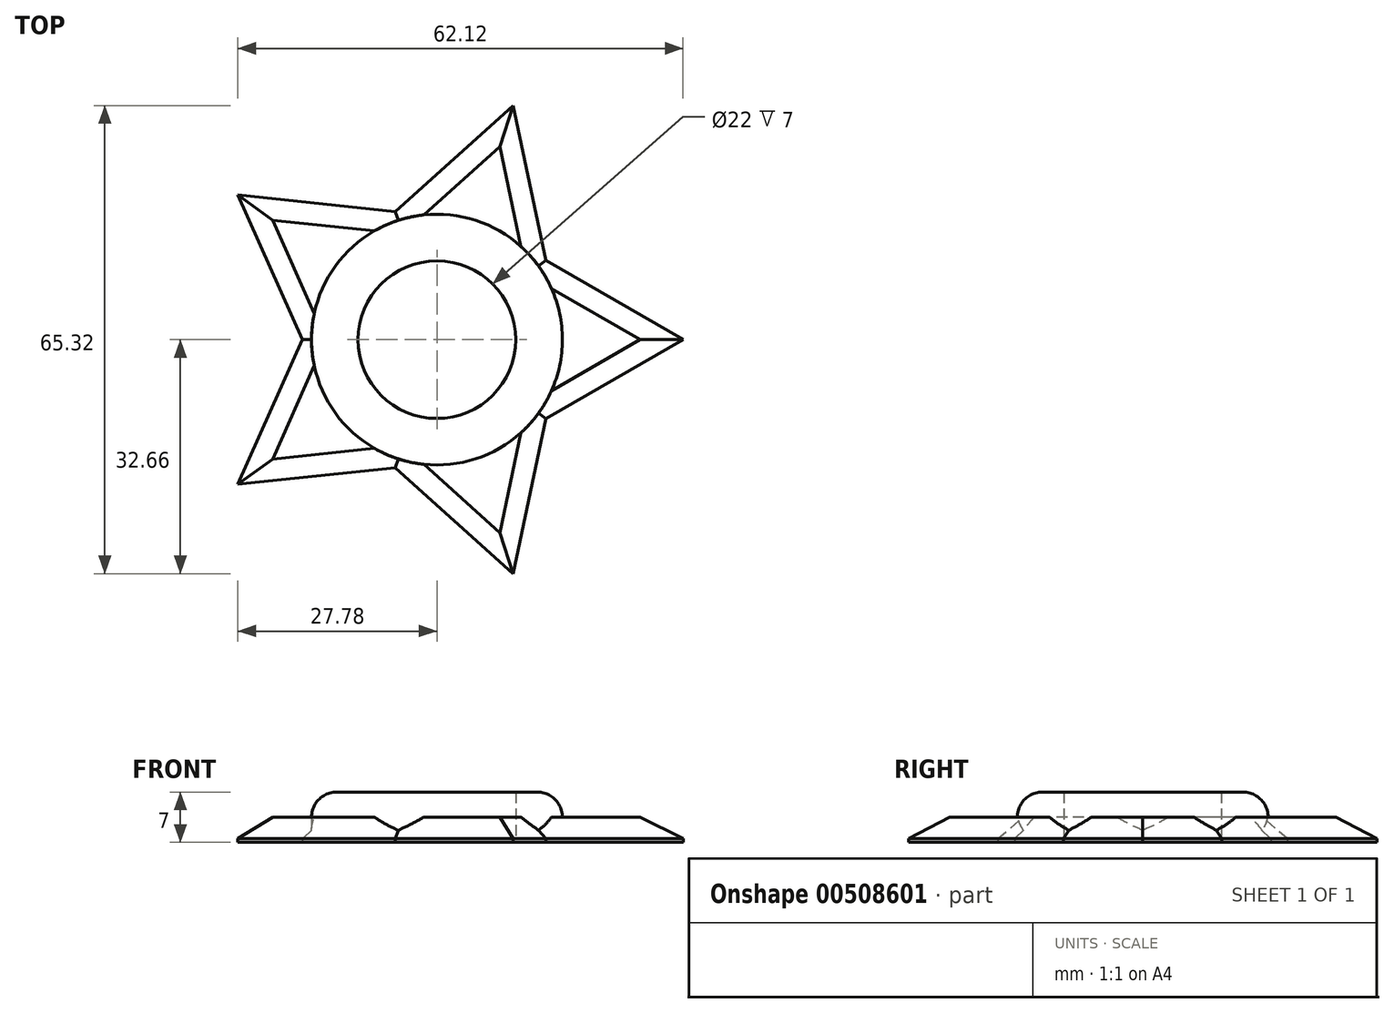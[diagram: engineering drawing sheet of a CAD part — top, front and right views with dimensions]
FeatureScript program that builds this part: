
annotation { "Feature Type Name" : "Feature", "Feature Type Description" : "" }
export const myFeature = defineFeature(function(context is Context, id is Id, definition is map)
    precondition{}
    {
        {
            var Q0;
            Q0=qCreatedBy(makeId("Top.planeOp"),FACE);
            var sketch = newSketch(context, id + "F0", { "sketchPlane" : qUnion([Q0])});
            skCircle(sketch, "E0", {"center": v(0, 0) * mm, "radius": 17.5 * mm});
            skCircle(sketch, "E1", {"center": v(0, 0) * mm, "radius": 11 * mm});
            skSolve(sketch);
        }
        {
            var Q0;
            Q0=makeQuery(id+"F0.imprint","IMPRINT",FACE,{"disambiguationData":[TD([[makeQuery(id+"F0.imprint","IMPRINT",EDGE,{"derivedFrom":sQuery(id+"F0.wireOp",EDGE,"E0")}),1.0]])]});
            extrude(context, id + "F1", {"entities" : qUnion([Q0]), "depth" : 7 * mm});
        }
        {
            var Q0;
            Q0=qCreatedBy(makeId("Top.planeOp"),FACE);
            var sketch = newSketch(context, id + "F2", { "sketchPlane" : qUnion([Q0])});
            skCircle(sketch, "E2.cCircle", {"center": v(18.8, 0) * mm, "radius": 7.77 * mm, "construction": true});
            skLineSegment(sketch, "E2.0", {"start": v(11.02, 13.46) * mm, "end": v(11.02, -13.46) * mm});
            skLineSegment(sketch, "E2.1", {"start": v(34.34, 0) * mm, "end": v(11.02, 13.46) * mm});
            skLineSegment(sketch, "E2.2", {"start": v(11.02, -13.46) * mm, "end": v(34.34, 0) * mm});
            skPoint(sketch, "E2.0.midPoint", {"position": v(11.02, 0) * mm});
            skLineSegment(sketch, "E3.1.0", {"start": v(16.21, 6.32) * mm, "end": v(10.61, 32.66) * mm});
            skLineSegment(sketch, "E3.1.1", {"start": v(10.61, 32.66) * mm, "end": v(-9.4, 14.64) * mm});
            skPoint(sketch, "E3.1.2", {"position": v(3.4, 10.48) * mm});
            skLineSegment(sketch, "E3.1.3", {"start": v(-9.4, 14.64) * mm, "end": v(16.21, 6.32) * mm});
            skCircle(sketch, "E3.1.4", {"center": v(5.8, 17.87) * mm, "radius": 7.77 * mm, "construction": true});
            skLineSegment(sketch, "E3.2.0", {"start": v(-1, 17.37) * mm, "end": v(-27.78, 20.19) * mm});
            skLineSegment(sketch, "E3.2.1", {"start": v(-27.78, 20.19) * mm, "end": v(-16.83, -4.42) * mm});
            skPoint(sketch, "E3.2.2", {"position": v(-8.92, 6.48) * mm});
            skLineSegment(sketch, "E3.2.3", {"start": v(-16.83, -4.42) * mm, "end": v(-1, 17.37) * mm});
            skCircle(sketch, "E3.2.4", {"center": v(-15.2, 11.05) * mm, "radius": 7.77 * mm, "construction": true});
            skLineSegment(sketch, "E3.3.0", {"start": v(-16.83, 4.42) * mm, "end": v(-27.78, -20.19) * mm});
            skLineSegment(sketch, "E3.3.1", {"start": v(-27.78, -20.19) * mm, "end": v(-1, -17.37) * mm});
            skPoint(sketch, "E3.3.2", {"position": v(-8.92, -6.48) * mm});
            skLineSegment(sketch, "E3.3.3", {"start": v(-1, -17.37) * mm, "end": v(-16.83, 4.42) * mm});
            skCircle(sketch, "E3.3.4", {"center": v(-15.2, -11.05) * mm, "radius": 7.77 * mm, "construction": true});
            skLineSegment(sketch, "E3.4.0", {"start": v(-9.4, -14.64) * mm, "end": v(10.61, -32.66) * mm});
            skLineSegment(sketch, "E3.4.1", {"start": v(10.61, -32.66) * mm, "end": v(16.21, -6.32) * mm});
            skPoint(sketch, "E3.4.2", {"position": v(3.4, -10.48) * mm});
            skLineSegment(sketch, "E3.4.3", {"start": v(16.21, -6.32) * mm, "end": v(-9.4, -14.64) * mm});
            skCircle(sketch, "E3.4.4", {"center": v(5.8, -17.87) * mm, "radius": 7.77 * mm, "construction": true});
            skPoint(sketch, "E3.center", {"position": v(0, 0) * mm});
            skSolve(sketch);
        }
        {
            var Q0;
            Q0 = qSketchRegion(id + "F2", true);
            extrude(context, id + "F3", {"entities" : qUnion([Q0]), "operationType" : NewBodyOperationType.ADD, "depth" : 3.5 * mm});
        }
        {
            var Q0;
            Q0=makeQuery(id+"F3.opExtrude","CAP_EDGE",EDGE,{"disambiguationData":[OSD([sQuery(id+"F2.wireOp",EDGE,"E3.1.0")])],"isStart":false});
            var Q1;
            Q1=makeQuery(id+"F3.opExtrude","CAP_EDGE",EDGE,{"disambiguationData":[OSD([sQuery(id+"F2.wireOp",EDGE,"E2.1")])],"isStart":false});
            var Q2;
            Q2=makeQuery(id+"F3.opExtrude","CAP_EDGE",EDGE,{"disambiguationData":[OSD([sQuery(id+"F2.wireOp",EDGE,"E2.2")])],"isStart":false});
            var Q3;
            Q3=makeQuery(id+"F3.opExtrude","CAP_EDGE",EDGE,{"disambiguationData":[OSD([sQuery(id+"F2.wireOp",EDGE,"E3.4.1")])],"isStart":false});
            var Q4;
            Q4=makeQuery(id+"F3.opExtrude","CAP_EDGE",EDGE,{"disambiguationData":[OSD([sQuery(id+"F2.wireOp",EDGE,"E3.4.0")])],"isStart":false});
            var Q5;
            Q5=makeQuery(id+"F3.opExtrude","CAP_EDGE",EDGE,{"disambiguationData":[OSD([sQuery(id+"F2.wireOp",EDGE,"E3.3.1")])],"isStart":false});
            var Q6;
            Q6=makeQuery(id+"F3.opExtrude","CAP_EDGE",EDGE,{"disambiguationData":[OSD([sQuery(id+"F2.wireOp",EDGE,"E3.3.0")])],"isStart":false});
            var Q7;
            Q7=makeQuery(id+"F3.opExtrude","CAP_EDGE",EDGE,{"disambiguationData":[OSD([sQuery(id+"F2.wireOp",EDGE,"E3.2.1")])],"isStart":false});
            var Q8;
            Q8=makeQuery(id+"F3.opExtrude","CAP_EDGE",EDGE,{"disambiguationData":[OSD([sQuery(id+"F2.wireOp",EDGE,"E3.2.0")])],"isStart":false});
            var Q9;
            Q9=makeQuery(id+"F3.opExtrude","CAP_EDGE",EDGE,{"disambiguationData":[OSD([sQuery(id+"F2.wireOp",EDGE,"E3.1.1")])],"isStart":false});
            chamfer(context, id + "F4", {"entities" : qUnion([Q0, Q1, Q2, Q3, Q4, Q5, Q6, Q7, Q8, Q9]), "width" : 3 * mm, "tangentPropagation" : true});
        }
        {
            var Q0;
            Q0=makeQuery(id+"F1.opExtrude","CAP_EDGE",EDGE,{"disambiguationData":[OSD([sQuery(id+"F0.wireOp",EDGE,"E0")])],"isStart":false});
            fillet(context, id + "F5", {"entities" : qUnion([Q0]), "radius" : 3.5 * mm, "tangentPropagation" : true, "allowEdgeOverflow" : false});
        }
    });
